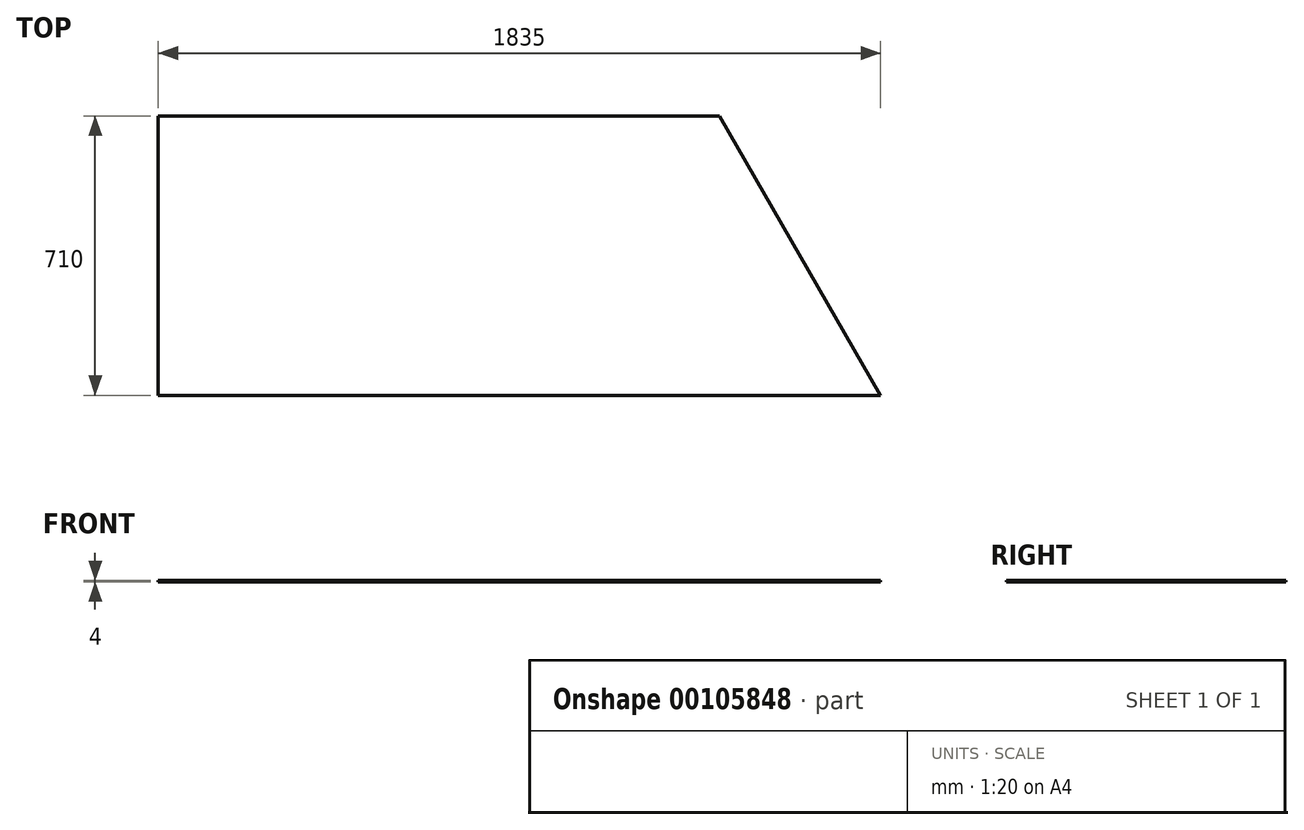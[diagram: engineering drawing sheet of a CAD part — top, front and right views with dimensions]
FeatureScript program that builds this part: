
annotation { "Feature Type Name" : "Feature", "Feature Type Description" : "" }
export const myFeature = defineFeature(function(context is Context, id is Id, definition is map)
    precondition{}
    {
        {
            var Q0;
            Q0=qCreatedBy(makeId("Top.planeOp"),FACE);
            var sketch = newSketch(context, id + "F0", { "sketchPlane" : qUnion([Q0])});
            skLineSegment(sketch, "E0", {"start": v(0, 0) * mm, "end": v(1835, 0) * mm});
            skLineSegment(sketch, "E1", {"start": v(0, 0) * mm, "end": v(0, 710) * mm});
            skLineSegment(sketch, "E2", {"start": v(0, 710) * mm, "end": v(1425, 710) * mm});
            skLineSegment(sketch, "E3", {"start": v(1425, 710) * mm, "end": v(1835, 0) * mm});
            skSolve(sketch);
        }
        {
            var Q0;
            Q0 = qSketchRegion(id + "F0", true);
            extrude(context, id + "F1", {"entities" : qUnion([Q0]), "depth" : 4 * mm});
        }
    });
